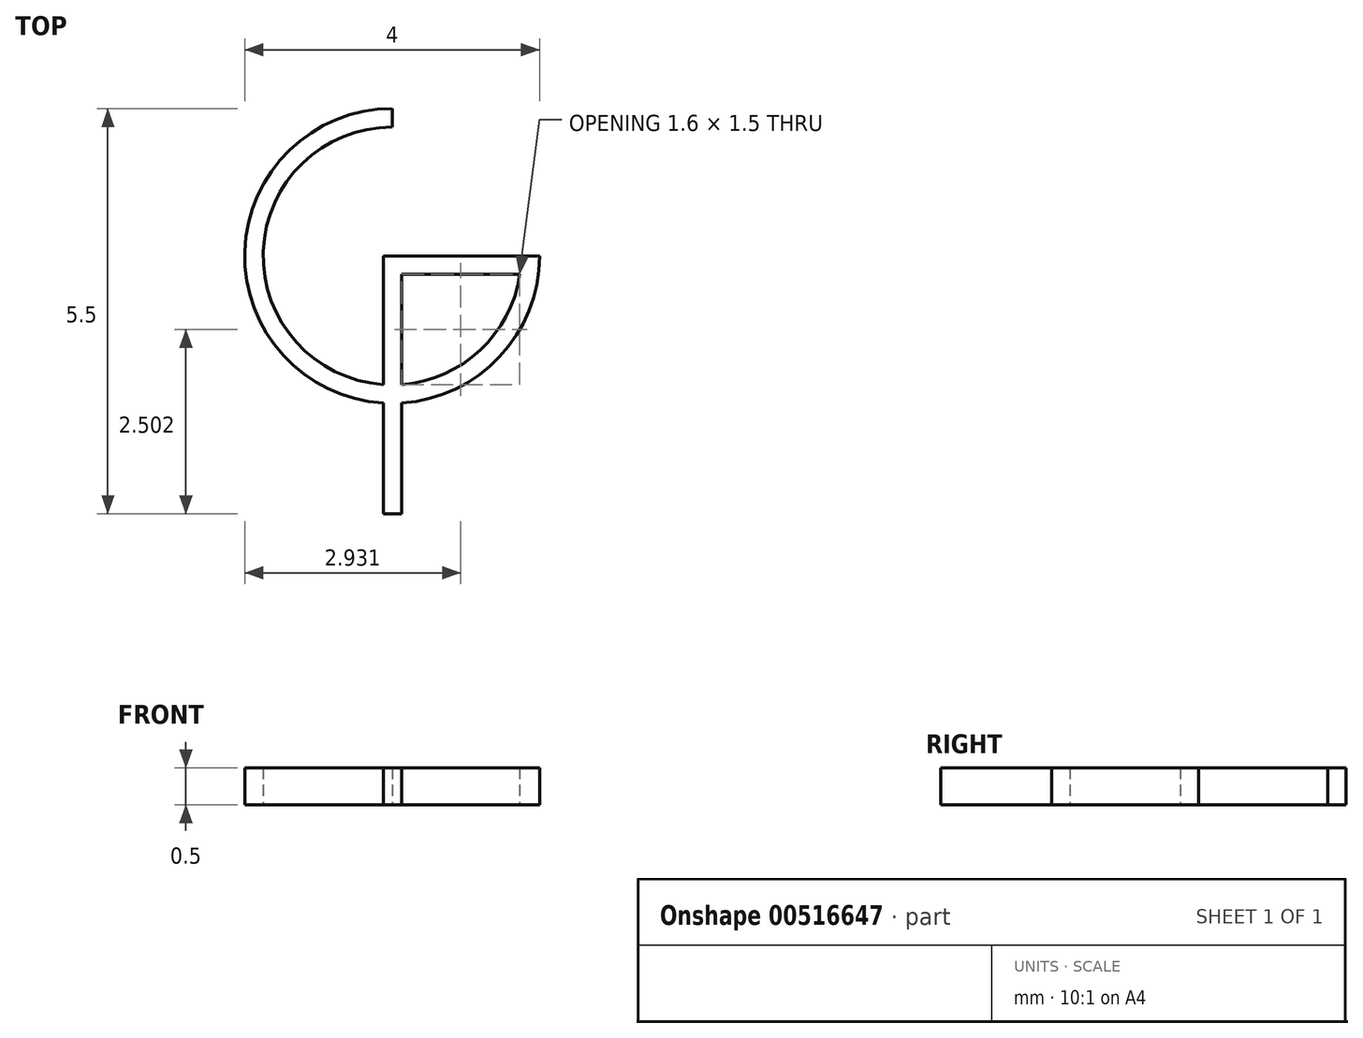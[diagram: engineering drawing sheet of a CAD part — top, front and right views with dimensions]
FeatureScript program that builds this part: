
annotation { "Feature Type Name" : "Feature", "Feature Type Description" : "" }
export const myFeature = defineFeature(function(context is Context, id is Id, definition is map)
    precondition{}
    {
        {
            var Q0;
            Q0=qCreatedBy(makeId("Top.planeOp"),FACE);
            var sketch = newSketch(context, id + "F0", { "sketchPlane" : qUnion([Q0])});
            skLineSegment(sketch, "E0.bottom", {"start": v(0, 0) * mm, "end": v(2, 0) * mm, "construction": true});
            skLineSegment(sketch, "E0.top", {"start": v(0, -2) * mm, "end": v(2, -2) * mm, "construction": true});
            skLineSegment(sketch, "E0.left", {"start": v(0, 0) * mm, "end": v(0, -2) * mm, "construction": true});
            skLineSegment(sketch, "E0.right", {"start": v(2, 0) * mm, "end": v(2, -2) * mm, "construction": true});
            skArc(sketch, "E1", {"start": v(0, 0) * mm, "mid": v(-1.41, -3.41) * mm, "end": v(2, -2) * mm});
            skLineSegment(sketch, "E2", {"start": v(0, 0) * mm, "end": v(0, -0.25) * mm});
            skLineSegment(sketch, "E3", {"start": v(2, -2) * mm, "end": v(1.75, -2) * mm});
            skArc(sketch, "E4", {"start": v(0, -0.25) * mm, "mid": v(-1.24, -3.24) * mm, "end": v(1.75, -2) * mm});
            skLineSegment(sketch, "E5", {"start": v(1.75, -2) * mm, "end": v(-0.12, -2) * mm});
            skLineSegment(sketch, "E6", {"start": v(-0.12, -2) * mm, "end": v(-0.12, -5.5) * mm});
            skLineSegment(sketch, "E7", {"start": v(-0.12, -5.5) * mm, "end": v(0.13, -5.5) * mm});
            skLineSegment(sketch, "E8", {"start": v(1.73, -2.25) * mm, "end": v(0.13, -2.25) * mm});
            skLineSegment(sketch, "E9", {"start": v(0.13, -2.25) * mm, "end": v(0.13, -5.5) * mm});
            skSolve(sketch);
        }
        {
            var Q0;
            {var subQ0=sQuery(id+"F0.wireOp",EDGE,"E2");Q0=makeQuery(id+"F0.imprint","IMPRINT",FACE,{"disambiguationData":[TD([[makeQuery(id+"F0.imprint","IMPRINT",EDGE,{"derivedFrom":subQ0}),-1.0]])]});}
            var Q1;
            {var subQ1=sQuery(id+"F0.wireOp",EDGE,"E5");Q1=makeQuery(id+"F0.imprint","IMPRINT",FACE,{"disambiguationData":[TD([[makeQuery(id+"F0.imprint","IMPRINT",EDGE,{"derivedFrom":subQ1}),1.0]])]});}
            var Q2;
            {var subQ1=sQuery(id+"F0.wireOp",EDGE,"E3");Q2=makeQuery(id+"F0.imprint","IMPRINT",FACE,{"disambiguationData":[TD([[makeQuery(id+"F0.imprint","IMPRINT",EDGE,{"derivedFrom":subQ1}),1.0]])]});}
            var Q3;
            {var subQ0=sQuery(id+"F0.wireOp",EDGE,"E6");var subQ1=sQuery(id+"F0.wireOp",EDGE,"E1");var subQ2=makeQuery(id+"F0.imprint","INTERSECT",VERTEX,{"derivedFrom":[subQ1,subQ0]});Q3=makeQuery(id+"F0.imprint","IMPRINT",FACE,{"disambiguationData":[TD([[makeQuery(id+"F0.imprint","IMPRINT",EDGE,{"disambiguationData":[TD([[subQ2,-1.0]])],"derivedFrom":subQ1}),1.0]])]});}
            var Q4;
            {var subQ5=sQuery(id+"F0.wireOp",EDGE,"E7");Q4=makeQuery(id+"F0.imprint","IMPRINT",FACE,{"disambiguationData":[TD([[makeQuery(id+"F0.imprint","IMPRINT",EDGE,{"derivedFrom":subQ5}),1.0]])]});}
            extrude(context, id + "F1", {"entities" : qUnion([Q0, Q1, Q2, Q3, Q4]), "depth" : 0.5 * mm, "offsetDistance" : 25 * mm});
        }
    });
